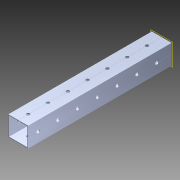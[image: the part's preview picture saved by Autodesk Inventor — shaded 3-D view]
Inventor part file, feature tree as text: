
AUTODESK INVENTOR PART (.ipt)
format: ipt  version: 2014 (Build 180170000, 170)  size: 1,142,272 bytes
history: native  units: in
note: dims shown in document units (in); Inventor stores cm internally (conversion verified against a paired STEP export)
features: pattern_circular x1, other x1, plane x1, extrude x1, imported_body x1, sketch x1
ambient origin geometry x8: Origin, YZ Plane, XZ Plane, XY Plane, X Axis, Y Axis, Z Axis, Center Point
bodies: Body1 (feature_tree)
feature tree (6):
  pattern_circular  "CirPattern2"
  other  "217-3426-STEP1"
  plane  "Work Plane1"
  extrude  "Extrusion1"  Depth=3937.0079in TaperAngle=0.0deg
  imported_body  "Base1"
  sketch  "Sketch1"  dims[d0=-6.125in d1=3937.0079in d2=0.0in]
